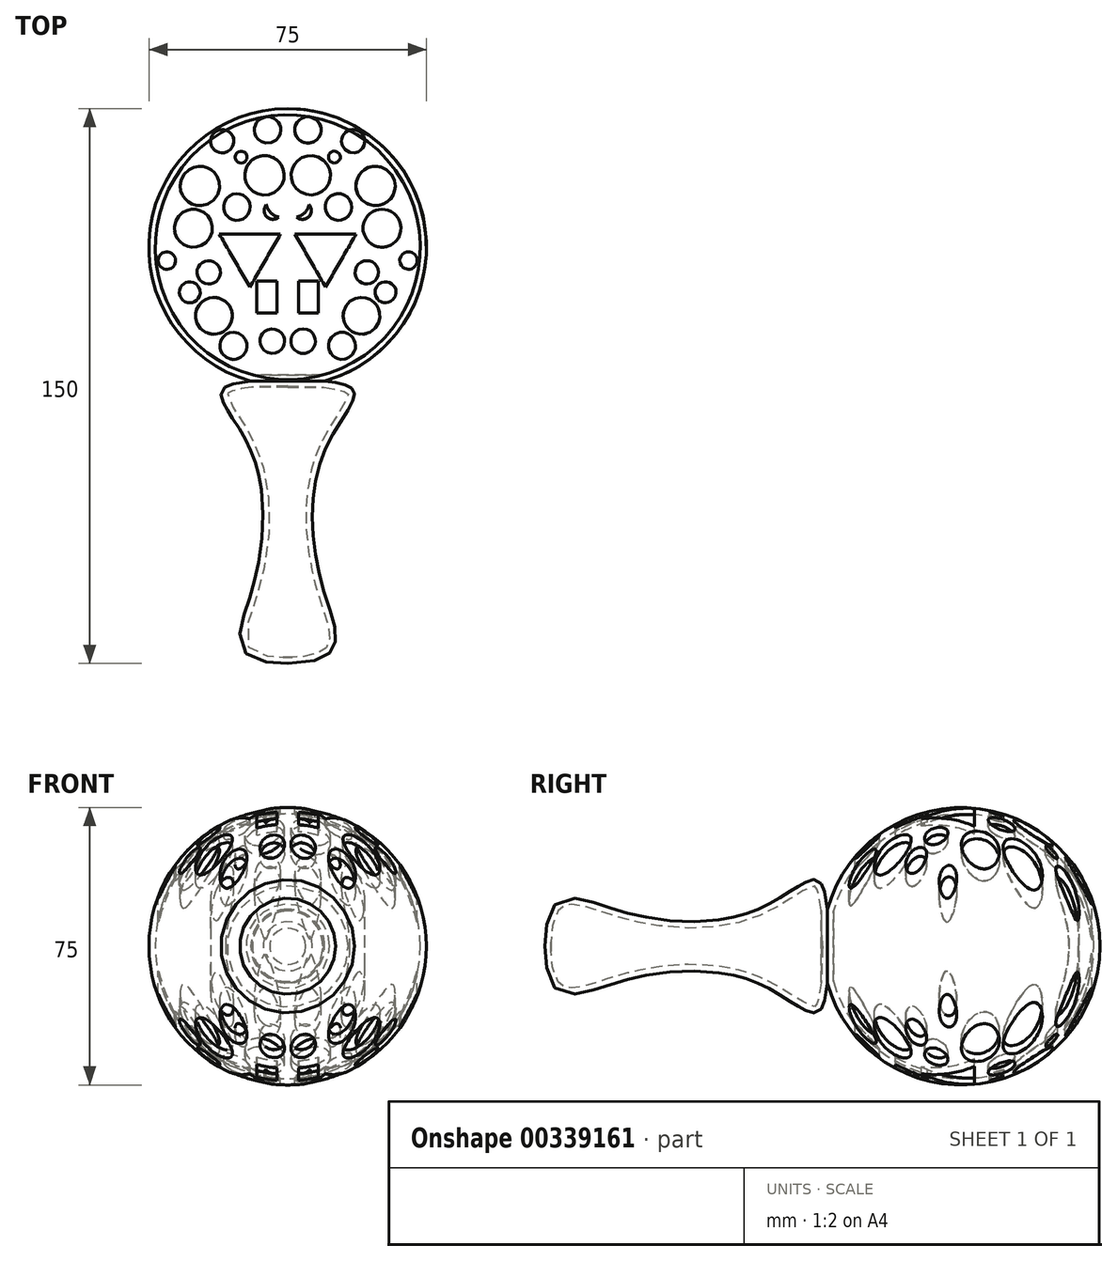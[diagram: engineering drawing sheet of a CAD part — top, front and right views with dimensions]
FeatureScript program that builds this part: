
annotation { "Feature Type Name" : "Feature", "Feature Type Description" : "" }
export const myFeature = defineFeature(function(context is Context, id is Id, definition is map)
    precondition{}
    {
        {
            var Q0;
            Q0=qCreatedBy(makeId("Top.planeOp"),FACE);
            var sketch = newSketch(context, id + "F0", { "sketchPlane" : qUnion([Q0])});
            skLineSegment(sketch, "E0.bottom", {"start": v(40, 75) * mm, "end": v(-40, 75) * mm, "construction": true});
            skLineSegment(sketch, "E0.top", {"start": v(40, -75) * mm, "end": v(-40, -75) * mm, "construction": true});
            skLineSegment(sketch, "E0.left", {"start": v(40, 75) * mm, "end": v(40, -75) * mm, "construction": true});
            skLineSegment(sketch, "E0.right", {"start": v(-40, 75) * mm, "end": v(-40, -75) * mm, "construction": true});
            skPoint(sketch, "E0.middle", {"position": v(0, 0) * mm});
            skLineSegment(sketch, "E1", {"start": v(0, 0) * mm, "end": v(0, 3) * mm, "construction": true});
            skPoint(sketch, "E2", {"position": v(0, 37.5) * mm});
            skArc(sketch, "E3", {"start": v(9.98, 1.35) * mm, "mid": v(37.16, 42.53) * mm, "end": v(0, 75) * mm});
            skFitSpline(sketch, "E4", {"points": [v(9.98, 1.35) * mm, v(17.95, -1.62) * mm, v(9.98, -17.45) * mm, v(9.98, -56.19) * mm, v(0, -75) * mm], "startDerivative": vector(69.5, -10.17) * mm, "endDerivative": vector(-209.68, 0) * mm});
            skFitSpline(sketch, "E5.0", {"points": [v(9.73, -0.33) * mm, v(10.46, -0.44) * mm, v(11.88, -0.64) * mm, v(13.47, -0.93) * mm, v(14.55, -1.2) * mm, v(15.24, -1.43) * mm, v(15.78, -1.66) * mm, v(16.13, -1.88) * mm, v(16.27, -2.02) * mm, v(16.3, -2.07) * mm, v(16.32, -2.1) * mm, v(16.32, -2.1) * mm, v(16.33, -2.14) * mm, v(16.34, -2.34) * mm, v(16.24, -2.79) * mm, v(16, -3.4) * mm, v(15.65, -4.16) * mm, v(15.02, -5.3) * mm, v(14, -6.96) * mm, v(12.51, -9.25) * mm, v(10.93, -11.82) * mm, v(9.63, -14.17) * mm, v(8.67, -16.17) * mm, v(7.79, -18.24) * mm, v(6.86, -20.94) * mm, v(6.01, -24.32) * mm, v(5.42, -27.82) * mm, v(5.06, -31.42) * mm, v(4.9, -36.31) * mm, v(5.18, -41.31) * mm, v(5.88, -46.34) * mm, v(6.47, -49.47) * mm, v(7.04, -51.96) * mm, v(7.52, -53.82) * mm, v(8.03, -55.66) * mm, v(8.6, -57.5) * mm, v(9.19, -59.28) * mm, v(9.95, -61.58) * mm, v(10.8, -64.28) * mm, v(11.25, -66.63) * mm, v(11.3, -68.2) * mm, v(11.17, -69.2) * mm, v(10.89, -70.02) * mm, v(10.44, -70.72) * mm, v(9.76, -71.37) * mm, v(8.74, -72) * mm, v(7.3, -72.54) * mm, v(4.75, -73.1) * mm, v(2.11, -73.3) * mm, v(0, -73.3) * mm]});
            skArc(sketch, "E6.0", {"start": v(9.53, 3) * mm, "mid": v(35.48, 42.3) * mm, "end": v(0, 73.3) * mm});
            skLineSegment(sketch, "E7", {"start": v(9.53, 3) * mm, "end": v(0, 3) * mm});
            skLineSegment(sketch, "E8", {"start": v(0, 3) * mm, "end": v(0, 0) * mm});
            skLineSegment(sketch, "E9", {"start": v(9.73, -0.33) * mm, "end": v(0, 0) * mm});
            skLineSegment(sketch, "E10", {"start": v(0, 75) * mm, "end": v(0, 73.3) * mm});
            skLineSegment(sketch, "E11", {"start": v(0, -73.3) * mm, "end": v(0, -75) * mm});
            skLineSegment(sketch, "E12.trimOffspring", {"start": v(0, 73.3) * mm, "end": v(0, 75) * mm, "construction": true});
            skLineSegment(sketch, "E13", {"start": v(0, 75) * mm, "end": v(0, 37.5) * mm, "construction": true});
            skSolve(sketch);
        }
        {
            var Q0;
            Q0=makeQuery(id+"F0.imprint","IMPRINT",FACE,{"disambiguationData":[TD([[makeQuery(id+"F0.imprint","IMPRINT",EDGE,{"derivedFrom":sQuery(id+"F0.wireOp",EDGE,"E3")}),1.0]])]});
            var Q1;
            Q1=sQuery(id+"F0.wireOp",EDGE,"E8");
            revolve(context, id + "F1", {"entities" : qUnion([Q0]), "axis" : qUnion([Q1]), "revolveType" : RevolveType.FULL});
        }
        {
            var Q0;
            Q0=qCreatedBy(makeId("Top.planeOp"),FACE);
            var sketch = newSketch(context, id + "F2", { "sketchPlane" : qUnion([Q0])});
            skCircle(sketch, "E14", {"center": v(5.45, 69.21) * mm, "radius": 3.57 * mm});
            skCircle(sketch, "E15", {"center": v(17.69, 66.2) * mm, "radius": 3.15 * mm});
            skCircle(sketch, "E16", {"center": v(6.24, 56.97) * mm, "radius": 5.31 * mm});
            skCircle(sketch, "E17", {"center": v(23.73, 54.1) * mm, "radius": 5.31 * mm});
            skCircle(sketch, "E18", {"center": v(4.18, 12.14) * mm, "radius": 3.32 * mm});
            skCircle(sketch, "E19", {"center": v(19.91, 18.97) * mm, "radius": 4.98 * mm});
            skCircle(sketch, "E20", {"center": v(14.67, 10.87) * mm, "radius": 3.66 * mm});
            skCircle(sketch, "E21", {"center": v(25.48, 42.66) * mm, "radius": 5.13 * mm});
            skCircle(sketch, "E22", {"center": v(26.43, 25.33) * mm, "radius": 2.83 * mm});
            skCircle(sketch, "E23.cCircle", {"center": v(10.22, 36.3) * mm, "radius": 4.77 * mm, "construction": true});
            skLineSegment(sketch, "E23.0", {"start": v(1.96, 41.07) * mm, "end": v(18.48, 41.07) * mm});
            skLineSegment(sketch, "E23.1", {"start": v(18.48, 41.07) * mm, "end": v(10.22, 26.76) * mm});
            skLineSegment(sketch, "E23.2", {"start": v(10.22, 26.76) * mm, "end": v(1.96, 41.07) * mm});
            skPoint(sketch, "E23.0.midPoint", {"position": v(10.22, 41.07) * mm});
            skLineSegment(sketch, "E24.bottom", {"start": v(2.9, 19.77) * mm, "end": v(8.3, 19.77) * mm});
            skLineSegment(sketch, "E24.top", {"start": v(2.9, 28.35) * mm, "end": v(8.3, 28.35) * mm});
            skLineSegment(sketch, "E24.left", {"start": v(2.9, 19.77) * mm, "end": v(2.9, 28.35) * mm});
            skLineSegment(sketch, "E24.right", {"start": v(8.3, 19.77) * mm, "end": v(8.3, 28.35) * mm});
            skPoint(sketch, "E24.middle", {"position": v(5.6, 24.06) * mm});
            skCircle(sketch, "E25", {"center": v(21.35, 30.74) * mm, "radius": 3.16 * mm});
            skCircle(sketch, "E26", {"center": v(13.71, 48.39) * mm, "radius": 3.6 * mm});
            skCircle(sketch, "E27", {"center": v(12.6, 61.9) * mm, "radius": 1.6 * mm});
            skCircle(sketch, "E28", {"center": v(32.63, 33.92) * mm, "radius": 2.36 * mm});
            skPoint(sketch, "E28.centerSnap0", {"position": v(6.09, 33.92) * mm});
            skArc(sketch, "E29", {"start": v(2.43, 45.68) * mm, "mid": v(5.69, 45.76) * mm, "end": v(5.77, 49.02) * mm});
            skArc(sketch, "E30", {"start": v(2.43, 45.68) * mm, "mid": v(4.6, 46.85) * mm, "end": v(5.77, 49.02) * mm});
            skCircle(sketch, "E31.MirrorC", {"center": v(-5.45, 69.21) * mm, "radius": 3.57 * mm});
            skCircle(sketch, "E32.MirrorC", {"center": v(-6.24, 56.97) * mm, "radius": 5.31 * mm});
            skCircle(sketch, "E33.MirrorC", {"center": v(-12.6, 61.9) * mm, "radius": 1.6 * mm});
            skCircle(sketch, "E34.MirrorC", {"center": v(-17.69, 66.2) * mm, "radius": 3.15 * mm});
            skCircle(sketch, "E35.MirrorC", {"center": v(-23.73, 54.1) * mm, "radius": 5.31 * mm});
            skCircle(sketch, "E36.MirrorC", {"center": v(-13.71, 48.39) * mm, "radius": 3.6 * mm});
            skArc(sketch, "E37.MirrorCS", {"start": v(-2.43, 45.68) * mm, "mid": v(-5.69, 45.76) * mm, "end": v(-5.77, 49.02) * mm});
            skArc(sketch, "E38.MirrorCS", {"start": v(-2.43, 45.68) * mm, "mid": v(-4.6, 46.85) * mm, "end": v(-5.77, 49.02) * mm});
            skLineSegment(sketch, "E39.MirrorCS", {"start": v(-1.96, 41.07) * mm, "end": v(-18.48, 41.07) * mm});
            skLineSegment(sketch, "E40.MirrorCS", {"start": v(-18.48, 41.07) * mm, "end": v(-10.22, 26.76) * mm});
            skLineSegment(sketch, "E41.MirrorCS", {"start": v(-10.22, 26.76) * mm, "end": v(-1.96, 41.07) * mm});
            skCircle(sketch, "E42.MirrorC", {"center": v(-10.22, 36.3) * mm, "radius": 4.77 * mm, "construction": true});
            skCircle(sketch, "E43.MirrorC", {"center": v(-25.48, 42.66) * mm, "radius": 5.13 * mm});
            skCircle(sketch, "E44.MirrorC", {"center": v(-32.63, 33.92) * mm, "radius": 2.36 * mm});
            skCircle(sketch, "E45.MirrorC", {"center": v(-21.35, 30.74) * mm, "radius": 3.16 * mm});
            skLineSegment(sketch, "E46.MirrorCS", {"start": v(-2.9, 28.35) * mm, "end": v(-8.3, 28.35) * mm});
            skLineSegment(sketch, "E47.MirrorCS", {"start": v(-8.3, 19.77) * mm, "end": v(-8.3, 28.35) * mm});
            skLineSegment(sketch, "E48.MirrorCS", {"start": v(-2.9, 19.77) * mm, "end": v(-8.3, 19.77) * mm});
            skLineSegment(sketch, "E49.MirrorCS", {"start": v(-2.9, 19.77) * mm, "end": v(-2.9, 28.35) * mm});
            skCircle(sketch, "E50.MirrorC", {"center": v(-14.67, 10.87) * mm, "radius": 3.66 * mm});
            skCircle(sketch, "E51.MirrorC", {"center": v(-4.18, 12.14) * mm, "radius": 3.32 * mm});
            skCircle(sketch, "E52.MirrorC", {"center": v(-19.91, 18.97) * mm, "radius": 4.98 * mm});
            skCircle(sketch, "E53.MirrorC", {"center": v(-26.43, 25.33) * mm, "radius": 2.83 * mm});
            skSolve(sketch);
        }
        {
            var Q0;
            Q0 = qSketchRegion(id + "F2", true);
            extrude(context, id + "F3", {"entities" : qUnion([Q0]), "operationType" : NewBodyOperationType.REMOVE, "endBound" : BoundingType.SYMMETRIC, "oppositeDirection" : true, "depth" : 120 * mm});
        }
    });
